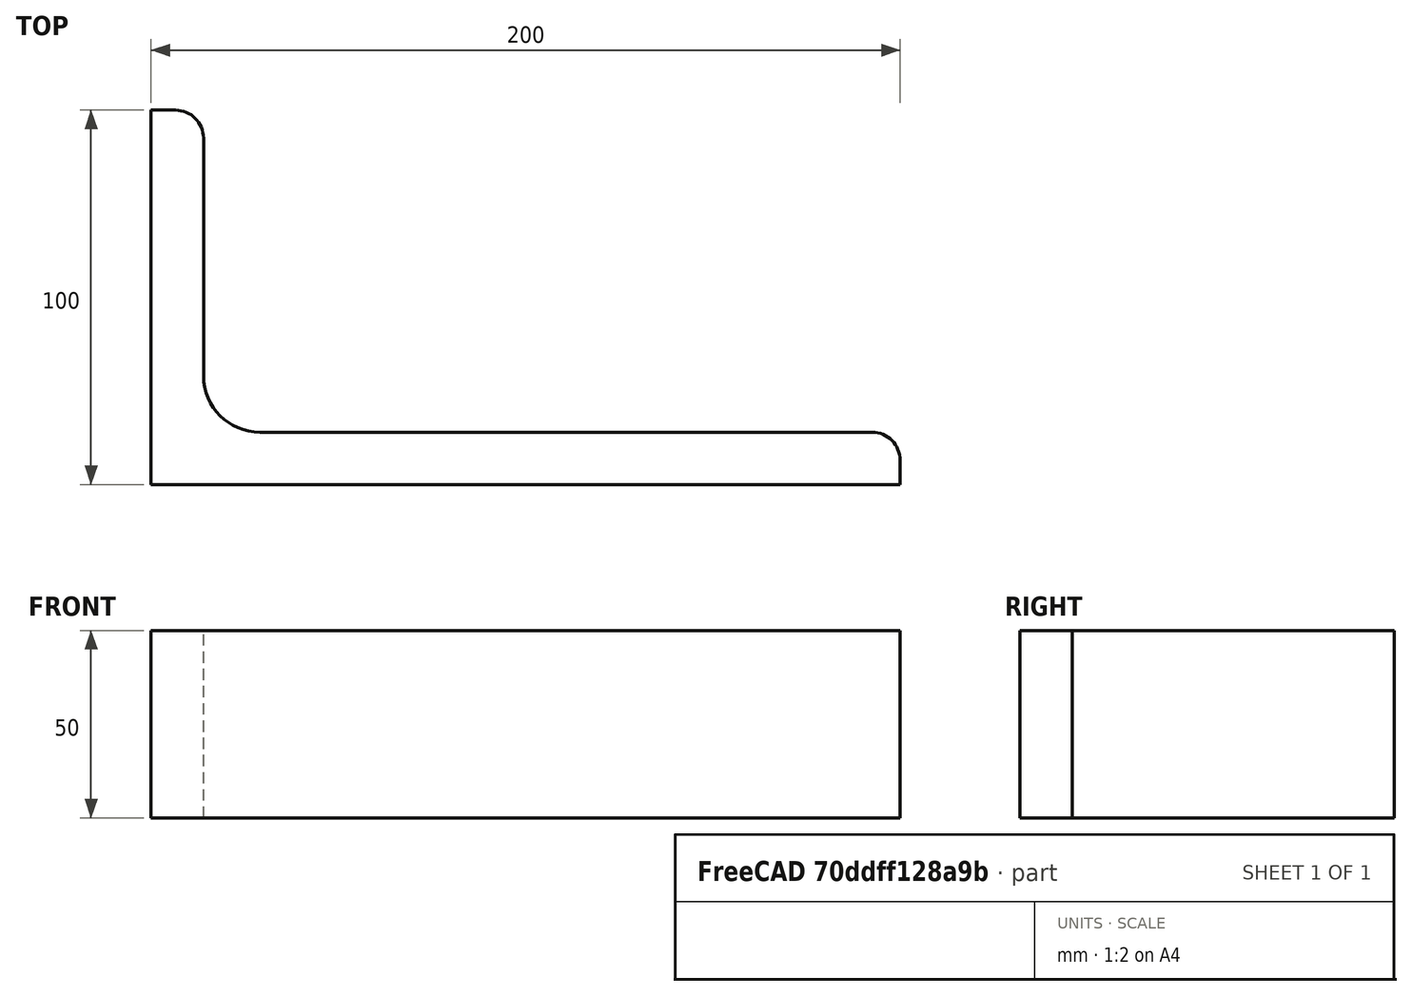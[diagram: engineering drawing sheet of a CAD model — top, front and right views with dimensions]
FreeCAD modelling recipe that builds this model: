
FCSTD DOCUMENT  (FreeCAD 0.15R4671 (Git))
Label: Angle Bar 200x100x14 EN10056 S235JR
License: All rights reserved
LicenseURL: http://en.wikipedia.org/wiki/All_rights_reserved
objects: Sketcher::SketchObject×1, Part::Extrusion×1
note: 2 computed .brp shape members not serialized (recipe doc carries the construction recipe); baked Part::Feature solids carry a one-line shape summary decoded from their .brp

FEATURE [Sketcher::SketchObject] Sketch
  sketch-geometry (9):
    g0: LineSegment StartX=0 StartY=0 StartZ=0 EndX=200 EndY=0 EndZ=0
    g1: LineSegment StartX=200 StartY=0 StartZ=0 EndX=200 EndY=6.5 EndZ=0
    g2: LineSegment StartX=192.5 StartY=14 StartZ=0 EndX=29 EndY=14 EndZ=0
    g3: LineSegment StartX=0 StartY=0 StartZ=0 EndX=0 EndY=100 EndZ=0
    g4: LineSegment StartX=0 StartY=100 StartZ=0 EndX=6.5 EndY=100 EndZ=0
    g5: LineSegment StartX=14 StartY=92.5 StartZ=0 EndX=14 EndY=29 EndZ=0
    g6: ArcOfCircle CenterX=29 CenterY=29 CenterZ=0 NormalX=0 NormalY=0 NormalZ=1 Radius=15 StartAngle=3.14159 EndAngle=4.71239
    g7: ArcOfCircle CenterX=6.5 CenterY=92.5 CenterZ=0 NormalX=0 NormalY=0 NormalZ=1 Radius=7.5 StartAngle=0 EndAngle=1.5708
    g8: ArcOfCircle CenterX=192.5 CenterY=6.5 CenterZ=0 NormalX=0 NormalY=0 NormalZ=1 Radius=7.5 StartAngle=0 EndAngle=1.5708
  constraints (23):
    c: Coincident(g0,g-1)
    c: Horizontal(g0)
    c: Coincident(g1,g0)
    c: Vertical(g1)
    c: Horizontal(g2)
    c: Coincident(g3,g-1)
    c: Vertical(g3)
    c: Coincident(g4,g3)
    c: Horizontal(g4)
    c: Vertical(g5)
    c: Tangent(g5,g6) = -1.5708
    c: Tangent(g2,g6) = 1.5708
    c: Tangent(g4,g7) = 1.5708
    c: Tangent(g5,g7) = 1.5708
    c: Tangent(g2,g8) = -1.5708
    c: Tangent(g1,g8) = -1.5708
    c: DistanceX(g0) = 200
    c: DistanceY(g3) = 100
    c: DistanceY(g0,g2) = 14
    c: DistanceX(g3,g5) = 14
    c: Radius(g6) = 15
    c: Radius(g8) = 7.5
    c: Radius(g7) = 7.5
FEATURE [Part::Extrusion] Extrude  label="Angle Bar 200x100x14 EN10056 S235JR"
  Base = -> Sketch
  Dir = (0,0,50)
  Solid = true
